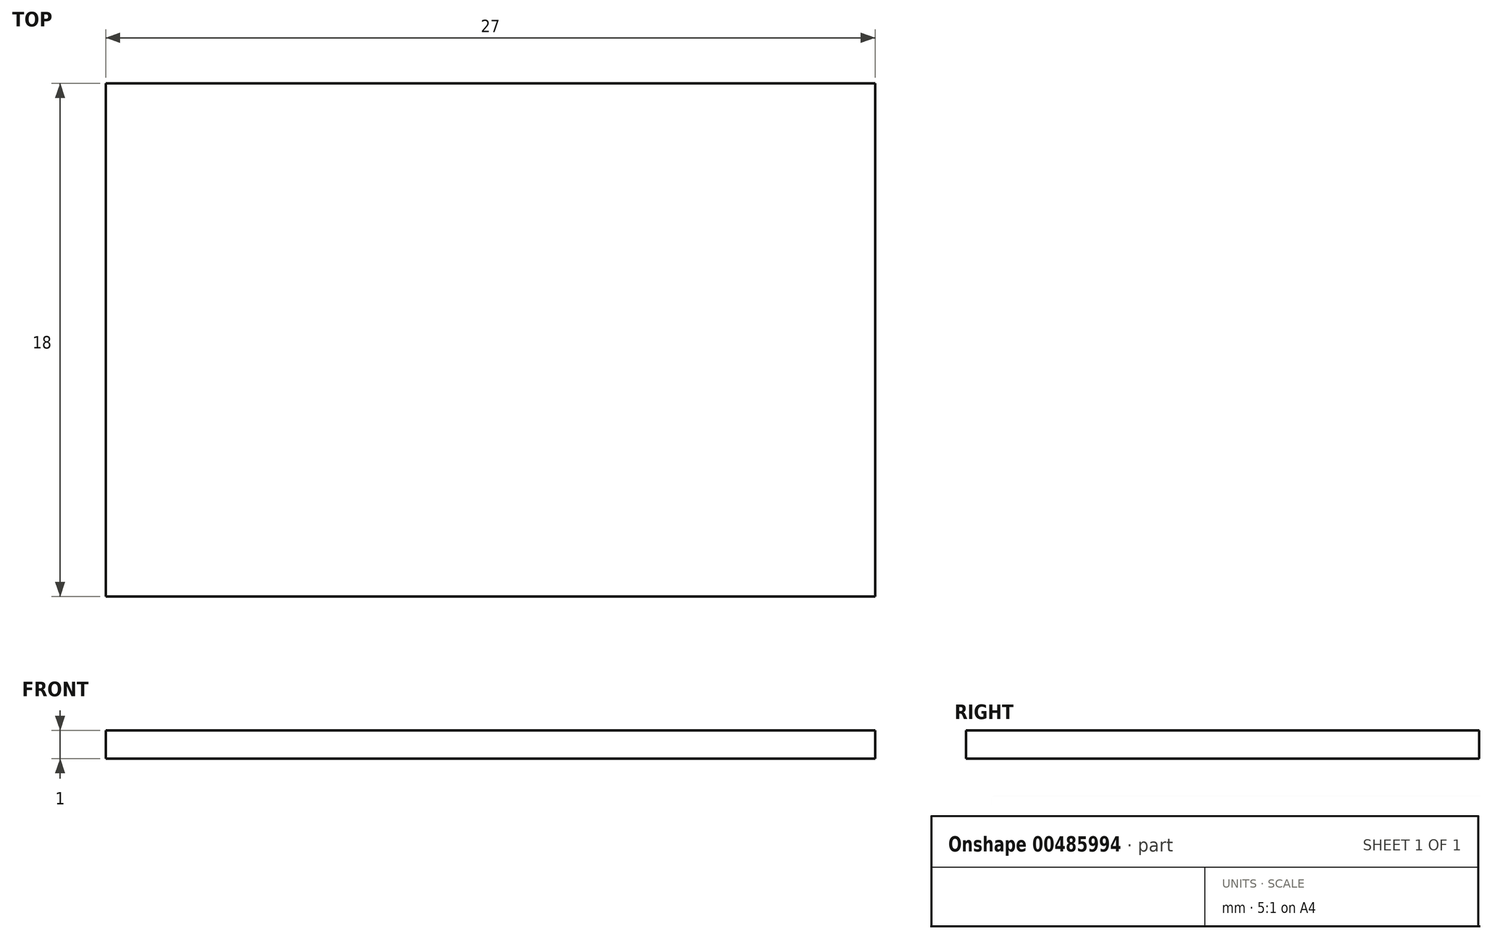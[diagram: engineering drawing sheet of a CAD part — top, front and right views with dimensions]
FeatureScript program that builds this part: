
annotation { "Feature Type Name" : "Feature", "Feature Type Description" : "" }
export const myFeature = defineFeature(function(context is Context, id is Id, definition is map)
    precondition{}
    {
        {
            var Q0;
            Q0=qCreatedBy(makeId("Top.planeOp"),FACE);
            var sketch = newSketch(context, id + "F0", { "sketchPlane" : qUnion([Q0])});
            skLineSegment(sketch, "E0.bottom", {"start": v(13.5, -9) * mm, "end": v(-13.5, -9) * mm});
            skLineSegment(sketch, "E0.top", {"start": v(13.5, 9) * mm, "end": v(-13.5, 9) * mm});
            skLineSegment(sketch, "E0.left", {"start": v(13.5, -9) * mm, "end": v(13.5, 9) * mm});
            skLineSegment(sketch, "E0.right", {"start": v(-13.5, -9) * mm, "end": v(-13.5, 9) * mm});
            skPoint(sketch, "E0.middle", {"position": v(0, 0) * mm});
            skSolve(sketch);
        }
        {
            var Q0;
            Q0 = qSketchRegion(id + "F0", true);
            extrude(context, id + "F1", {"entities" : qUnion([Q0]), "depth" : 1 * mm});
        }
    });
